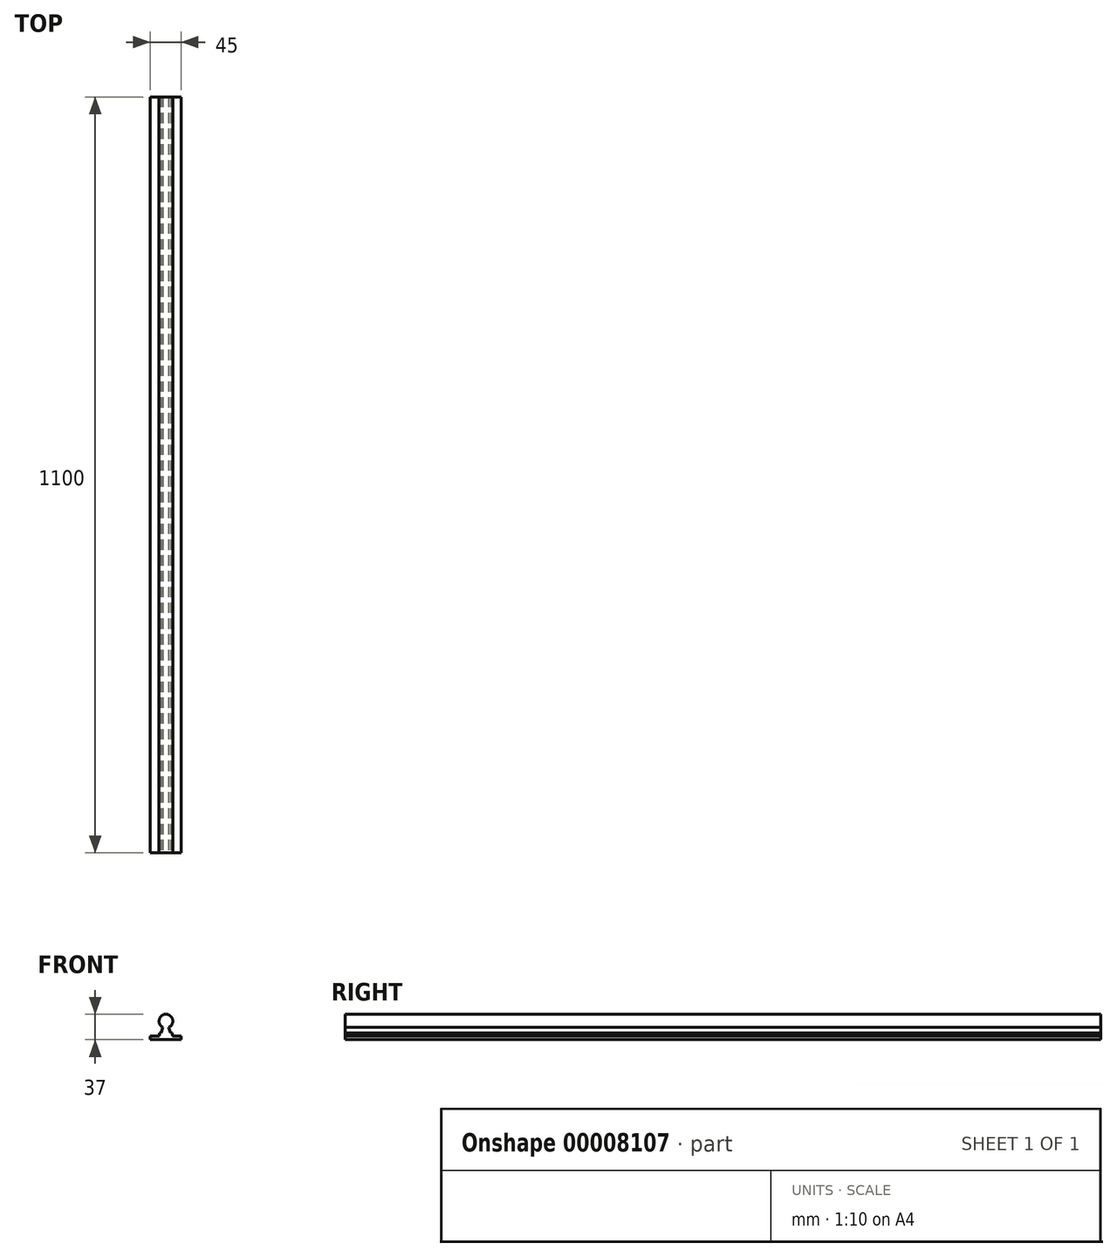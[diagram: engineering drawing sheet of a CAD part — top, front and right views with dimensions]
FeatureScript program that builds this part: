
annotation { "Feature Type Name" : "Feature", "Feature Type Description" : "" }
export const myFeature = defineFeature(function(context is Context, id is Id, definition is map)
    precondition{}
    {
        {
            var Q0;
            Q0=qCreatedBy(makeId("Front.planeOp"),FACE);
            var sketch = newSketch(context, id + "F0", { "sketchPlane" : qUnion([Q0])});
            skLineSegment(sketch, "E0", {"start": v(-22.53, -8.74) * mm, "end": v(22.47, -8.74) * mm});
            skLineSegment(sketch, "E1", {"start": v(22.47, -3.74) * mm, "end": v(9.47, -3.74) * mm});
            skLineSegment(sketch, "E2", {"start": v(9.47, -3.74) * mm, "end": v(9.47, 1.26) * mm});
            skLineSegment(sketch, "E3", {"start": v(6.97, 1.26) * mm, "end": v(4.02, 8.99) * mm});
            skLineSegment(sketch, "E4", {"start": v(-9.53, -3.74) * mm, "end": v(-9.53, 1.26) * mm});
            skLineSegment(sketch, "E5", {"start": v(-22.53, -3.74) * mm, "end": v(-9.53, -3.74) * mm});
            skLineSegment(sketch, "E6", {"start": v(-7.03, 1.26) * mm, "end": v(-3.98, 9.22) * mm});
            skCircle(sketch, "E7", {"center": v(0.28, 18.26) * mm, "radius": 10 * mm});
            skLineSegment(sketch, "E8", {"start": v(22.47, -8.74) * mm, "end": v(22.47, -3.74) * mm});
            skLineSegment(sketch, "E9", {"start": v(-22.53, -8.74) * mm, "end": v(-22.53, -3.74) * mm});
            skLineSegment(sketch, "E10", {"start": v(-9.53, 1.26) * mm, "end": v(-7.03, 1.26) * mm});
            skLineSegment(sketch, "E11", {"start": v(9.47, 1.26) * mm, "end": v(6.97, 1.26) * mm});
            skSolve(sketch);
        }
        {
            var Q0;
            {var subQ0=sQuery(id+"F0.wireOp",EDGE,"E7");var subQ2=makeQuery(id+"F0.imprint","INTERSECT",VERTEX,{"derivedFrom":[sQuery(id+"F0.wireOp",EDGE,"E3"),subQ0]});Q0=makeQuery(id+"F0.imprint","IMPRINT",FACE,{"disambiguationData":[TD([[makeQuery(id+"F0.imprint","IMPRINT",EDGE,{"disambiguationData":[TD([[subQ2,1.0]])],"derivedFrom":subQ0}),1.0]])]});}
            var Q1;
            Q1=makeQuery(id+"F0.imprint","IMPRINT",FACE,{"disambiguationData":[TD([[makeQuery(id+"F0.imprint","IMPRINT",EDGE,{"derivedFrom":sQuery(id+"F0.wireOp",EDGE,"E0")}),1.0]])]});
            extrude(context, id + "F1", {"entities" : qUnion([Q0, Q1]), "oppositeDirection" : true, "depth" : 1100 * mm});
        }
    });
